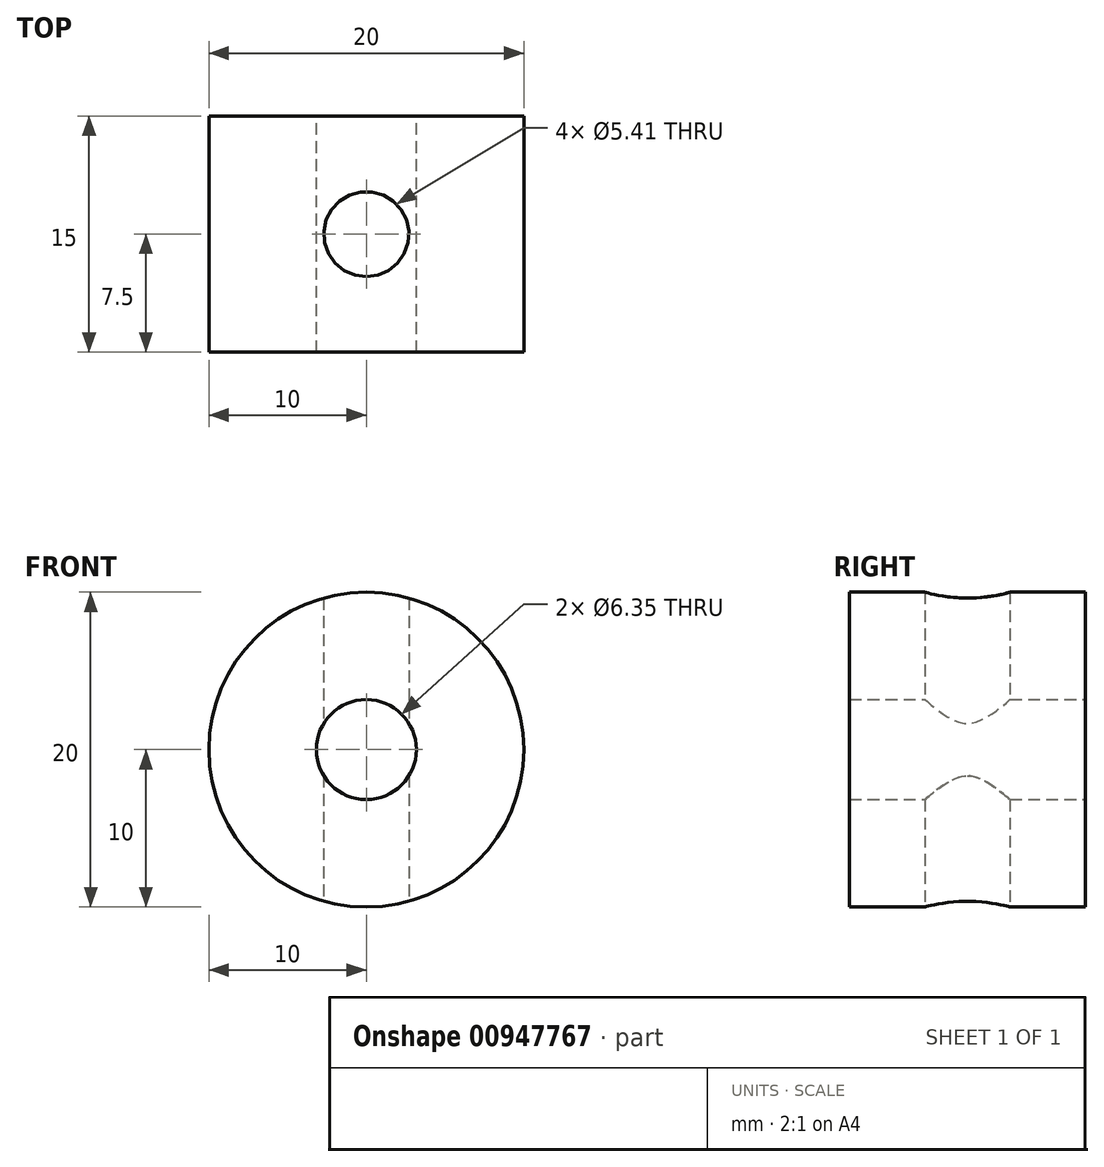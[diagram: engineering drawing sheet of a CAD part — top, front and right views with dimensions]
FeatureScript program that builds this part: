
annotation { "Feature Type Name" : "Feature", "Feature Type Description" : "" }
export const myFeature = defineFeature(function(context is Context, id is Id, definition is map)
    precondition{}
    {
        {
            var Q0;
            Q0=qCreatedBy(makeId("Front.planeOp"),FACE);
            var sketch = newSketch(context, id + "F0", { "sketchPlane" : qUnion([Q0])});
            skCircle(sketch, "E0", {"center": v(0, 0) * mm, "radius": 10 * mm});
            skCircle(sketch, "E1", {"center": v(0, 0) * mm, "radius": 3.17 * mm});
            skSolve(sketch);
        }
        {
            var Q0;
            Q0 = qSketchRegion(id + "F0", true);
            extrude(context, id + "F1", {"entities" : qUnion([Q0]), "depth" : 15 * mm, "offsetDistance" : 25 * mm, "symmetric" : true});
        }
        {
            var Q0;
            Q0=qCreatedBy(makeId("Top.planeOp"),FACE);
            cPlane(context, id + "F2", {"entities" : qUnion([Q0]), "cplaneType" : CPlaneType.OFFSET, "offset" : 12.7 * mm, "width" : 150 * mm, "height" : 150 * mm});
        }
        {
            var Q0;
            Q0=qCreatedBy(id+"F2.planeOp",FACE);
            var sketch = newSketch(context, id + "F3", { "sketchPlane" : qUnion([Q0])});
            skPoint(sketch, "E2", {"position": v(0, 0) * mm});
            skSolve(sketch);
        }
        {
            var Q0;
            Q0=sQuery(id+"F3.wireOp",VERTEX,"E2");
            var Q1;
            Q1=makeQuery(id+"F1.opExtrude","SWEPT_BODY",BODY,{"disambiguationData":[OSD([sQuery(id+"F0.wireOp",EDGE,"E0"),sQuery(id+"F0.wireOp",EDGE,"E1")])]});
            hole(context, id + "F4", {"style" : HoleStyle.SIMPLE, "endStyle" : HoleEndStyle.THROUGH, "standardTappedOrClearance" : lookupTablePath({ "standard" : "ANSI", "engagement" : "75%", "pitch" : "28 tpi", "size" : "1/4", "type" : "Tapped" }), "standardBlindInLast" : lookupTablePath({ "standard" : "ANSI", "fit" : "Normal", "engagement" : "75%", "pitch" : "28 tpi", "size" : "1/4", "type" : "Clearance & tapped" }), "holeDiameter" : 5.4 * mm, "majorDiameter" : 6.35 * mm, "showTappedDepth" : true, "isTappedThrough" : true, "tappedDepth" : 25.4 * mm, "tapClearance" : 3, "locations" : qUnion([Q0]), "scope" : qUnion([Q1]), "startStyle" : HoleStartStyle.SKETCH});
        }
    });
